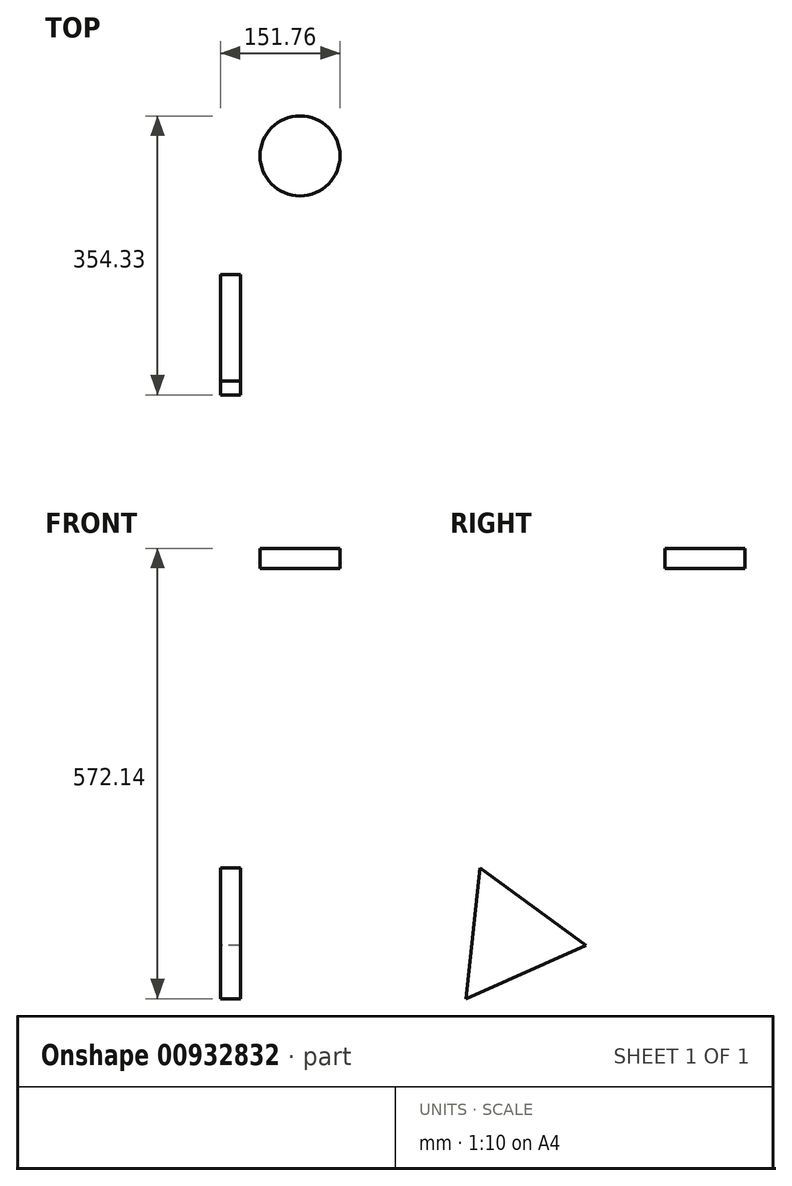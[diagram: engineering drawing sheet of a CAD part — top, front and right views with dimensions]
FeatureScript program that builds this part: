
annotation { "Feature Type Name" : "Feature", "Feature Type Description" : "" }
export const myFeature = defineFeature(function(context is Context, id is Id, definition is map)
    precondition{}
    {
        {
            var Q0;
            Q0=qCreatedBy(makeId("Top.planeOp"),FACE);
            var sketch = newSketch(context, id + "F0", { "sketchPlane" : qUnion([Q0])});
            skLineSegment(sketch, "E0", {"start": v(-178.88, 32.33) * mm, "end": v(22.06, 62.52) * mm});
            skLineSegment(sketch, "E1.bottom", {"start": v(-123.3, 11.6) * mm, "end": v(-61.34, 11.6) * mm});
            skLineSegment(sketch, "E1.top", {"start": v(-123.3, -20.02) * mm, "end": v(-61.34, -20.02) * mm});
            skLineSegment(sketch, "E1.left", {"start": v(-123.3, 11.6) * mm, "end": v(-123.3, -20.02) * mm});
            skLineSegment(sketch, "E1.right", {"start": v(-61.34, 11.6) * mm, "end": v(-61.34, -20.02) * mm});
            skLineSegment(sketch, "E2.bottom", {"start": v(-27.61, 14.54) * mm, "end": v(27.61, 14.54) * mm});
            skLineSegment(sketch, "E2.top", {"start": v(-27.61, -14.54) * mm, "end": v(27.61, -14.54) * mm});
            skLineSegment(sketch, "E2.left", {"start": v(-27.61, 14.54) * mm, "end": v(-27.61, -14.54) * mm});
            skLineSegment(sketch, "E2.right", {"start": v(27.61, 14.54) * mm, "end": v(27.61, -14.54) * mm});
            skPoint(sketch, "E2.middle", {"position": v(0, 0) * mm});
            skCircle(sketch, "E3", {"center": v(100.96, 22.13) * mm, "radius": 50.8 * mm});
            skArc(sketch, "E4", {"start": v(0, 23.82) * mm, "mid": v(92.64, 12.99) * mm, "end": v(99.28, 106.02) * mm});
            skSolve(sketch);
        }
        {
            var Q0;
            {var subQ0=sQuery(id+"F0.wireOp",EDGE,"E4");var subQ1=sQuery(id+"F0.wireOp",EDGE,"E3");var subQ2=makeQuery(id+"F0.imprint","INTERSECT",VERTEX,{"disambiguationData":[OD(0.0)],"derivedFrom":[subQ1,subQ0]});Q0=makeQuery(id+"F0.imprint","IMPRINT",FACE,{"disambiguationData":[TD([[makeQuery(id+"F0.imprint","IMPRINT",EDGE,{"disambiguationData":[TD([[subQ2,1.0]])],"derivedFrom":subQ1}),1.0]])]});}
            var Q1;
            {var subQ0=sQuery(id+"F0.wireOp",EDGE,"E4");var subQ1=sQuery(id+"F0.wireOp",EDGE,"E3");var subQ2=makeQuery(id+"F0.imprint","INTERSECT",VERTEX,{"disambiguationData":[OD(0.0)],"derivedFrom":[subQ1,subQ0]});Q1=makeQuery(id+"F0.imprint","IMPRINT",FACE,{"disambiguationData":[TD([[makeQuery(id+"F0.imprint","IMPRINT",EDGE,{"disambiguationData":[TD([[subQ2,-1.0]])],"derivedFrom":subQ1}),1.0]])]});}
            extrude(context, id + "F1", {"entities" : qUnion([Q0, Q1]), "oppositeDirection" : true, "depth" : 25.4 * mm, "offsetDistance" : 25.4 * mm});
        }
        {
            var Q0;
            Q0=qCreatedBy(makeId("Right.planeOp"),FACE);
            var sketch = newSketch(context, id + "F2", { "sketchPlane" : qUnion([Q0])});
            skCircle(sketch, "E5.cCircle", {"center": v(-224.69, -494.2) * mm, "radius": 48.2 * mm, "construction": true});
            skLineSegment(sketch, "E5.0", {"start": v(-263.82, -406.13) * mm, "end": v(-128.84, -504.35) * mm});
            skLineSegment(sketch, "E5.1", {"start": v(-128.84, -504.35) * mm, "end": v(-281.4, -572.14) * mm});
            skLineSegment(sketch, "E5.2", {"start": v(-281.4, -572.14) * mm, "end": v(-263.82, -406.13) * mm});
            skPoint(sketch, "E5.0.midPoint", {"position": v(-196.33, -455.24) * mm});
            skFitSpline(sketch, "E6", {"points": [v(-187.24, -367.53) * mm, v(-160.8, -382.92) * mm, v(-147.1, -350.48) * mm, v(-142.1, -311.3) * mm, v(-164.4, -314.9) * mm, v(-191.12, -327.1) * mm, v(-159.88, -278.1) * mm, v(-140.43, -201.06) * mm, v(-197.42, -231.08) * mm, v(-203.93, -356.6) * mm], "startDerivative": vector(345.25, -301.71) * mm, "endDerivative": vector(130.77, -797.7) * mm});
            skText(sketch, "E7", { "text": "Default textjsj", "fontName": "OpenSans-Regular.ttf"});
            const initialGuessF2  = {"E7": [-0.0376, -0.25605, 1, 0, 0.07324]};
            skSetInitialGuess(sketch, initialGuessF2);
            skSolve(sketch);
        }
        {
            var Q0;
            Q0=makeQuery(id+"F2.imprint","IMPRINT",FACE,{"disambiguationData":[TD([[makeQuery(id+"F2.imprint","IMPRINT",EDGE,{"derivedFrom":sQuery(id+"F2.wireOp",EDGE,"E5.0")}),-1.0]])]});
            extrude(context, id + "F3", {"entities" : qUnion([Q0]), "depth" : 25.4 * mm, "offsetDistance" : 25.4 * mm});
        }
    });
